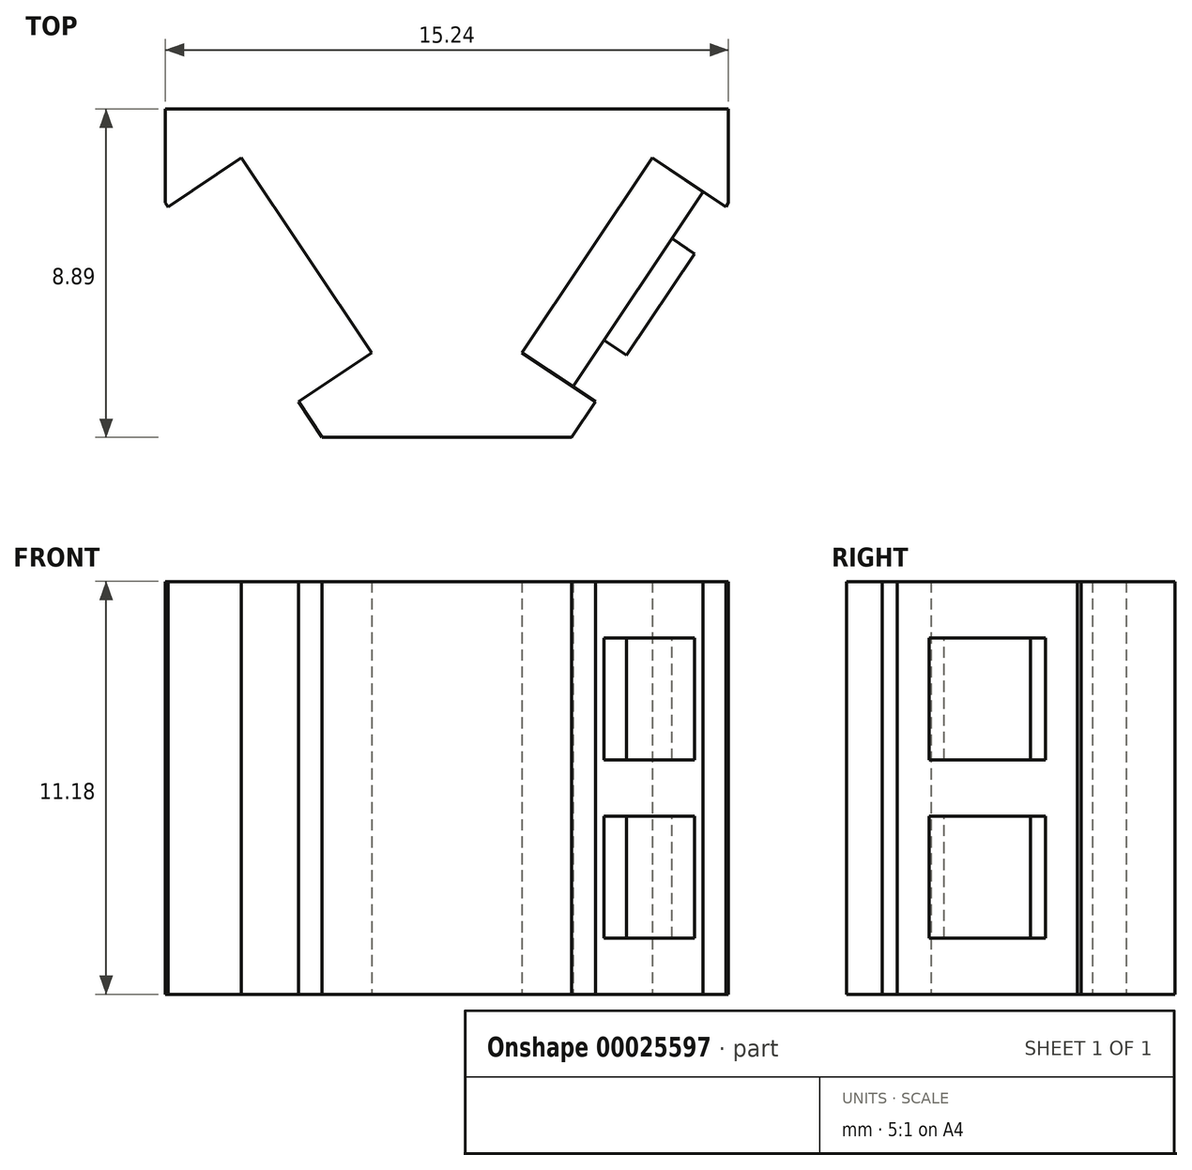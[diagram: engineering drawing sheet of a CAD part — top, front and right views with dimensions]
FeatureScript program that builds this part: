
annotation { "Feature Type Name" : "Feature", "Feature Type Description" : "" }
export const myFeature = defineFeature(function(context is Context, id is Id, definition is map)
    precondition{}
    {
        {
            var Q0;
            Q0=qCreatedBy(makeId("Top.planeOp"),FACE);
            var sketch = newSketch(context, id + "F0", { "sketchPlane" : qUnion([Q0])});
            skLineSegment(sketch, "E0", {"start": v(0, 0) * mm, "end": v(7.62, 0) * mm});
            skLineSegment(sketch, "E1", {"start": v(7.62, 0) * mm, "end": v(7.62, -2.54) * mm});
            skLineSegment(sketch, "E2", {"start": v(7.62, -2.54) * mm, "end": v(7.55, -2.65) * mm});
            skLineSegment(sketch, "E3", {"start": v(3.38, -8.9) * mm, "end": v(0, -8.9) * mm});
            skLineSegment(sketch, "E4", {"start": v(0, -8.9) * mm, "end": v(0, 0) * mm});
            skLineSegment(sketch, "E5", {"start": v(4.02, -7.93) * mm, "end": v(2.03, -6.6) * mm});
            skLineSegment(sketch, "E6", {"start": v(2.03, -6.6) * mm, "end": v(5.56, -1.32) * mm});
            skLineSegment(sketch, "E7", {"start": v(5.56, -1.32) * mm, "end": v(7.55, -2.65) * mm});
            skLineSegment(sketch, "E8.trimOffspring", {"start": v(4.02, -7.93) * mm, "end": v(3.38, -8.89) * mm});
            skSolve(sketch);
        }
        {
            var Q0;
            Q0=makeQuery(id+"F0.imprint","IMPRINT",FACE,{"disambiguationData":[TD([[makeQuery(id+"F0.imprint","IMPRINT",EDGE,{"derivedFrom":sQuery(id+"F0.wireOp",EDGE,"E0")}),-1.0]])]});
            extrude(context, id + "F1", {"entities" : qUnion([Q0]), "depth" : 11.18 * mm});
        }
        {
            var Q0;
            Q0=makeQuery(id+"F1.opExtrude","SWEPT_BODY",BODY,{"disambiguationData":[OSD([sQuery(id+"F0.wireOp",EDGE,"E0"),sQuery(id+"F0.wireOp",EDGE,"E1"),sQuery(id+"F0.wireOp",EDGE,"E2"),sQuery(id+"F0.wireOp",EDGE,"E3"),sQuery(id+"F0.wireOp",EDGE,"E4"),sQuery(id+"F0.wireOp",EDGE,"E5"),sQuery(id+"F0.wireOp",EDGE,"E6"),sQuery(id+"F0.wireOp",EDGE,"E7"),sQuery(id+"F0.wireOp",EDGE,"E8.trimOffspring")])]});
            var Q1;
            Q1=qCreatedBy(makeId("Right.planeOp"),FACE);
            mirror(context, id + "F2", {"operationType" : NewBodyOperationType.ADD, "entities" : qUnion([Q0]), "mirrorPlane" : qUnion([Q1])});
        }
        {
            var Q0;
            Q0=makeQuery(id+"F1.opExtrude","SWEPT_FACE",FACE,{"disambiguationData":[OSD([sQuery(id+"F0.wireOp",EDGE,"E6")])]});
            var sketch = newSketch(context, id + "F3", { "sketchPlane" : qUnion([Q0])});
            skLineSegment(sketch, "E9.bottom", {"start": v(-4.36, 0) * mm, "end": v(2, 0) * mm});
            skLineSegment(sketch, "E9.top", {"start": v(-4.36, 11.18) * mm, "end": v(2, 11.18) * mm});
            skLineSegment(sketch, "E9.left", {"start": v(-4.36, 0) * mm, "end": v(-4.36, 11.18) * mm});
            skLineSegment(sketch, "E9.right", {"start": v(2, 0) * mm, "end": v(2, 11.18) * mm});
            skSolve(sketch);
        }
        {
            var Q0;
            Q0=makeQuery(id+"F3.imprint","IMPRINT",FACE,{"disambiguationData":[TD([[makeQuery(id+"F3.imprint","IMPRINT",EDGE,{"derivedFrom":sQuery(id+"F3.wireOp",EDGE,"E9.bottom")}),1.0]])]});
            extrude(context, id + "F4", {"entities" : qUnion([Q0]), "depth" : 1.65 * mm});
        }
        {
            var Q0;
            Q0=makeQuery(id+"F4.opExtrude","CAP_FACE",FACE,{"disambiguationData":[OSD([sQuery(id+"F3.wireOp",EDGE,"E9.bottom"),sQuery(id+"F3.wireOp",EDGE,"E9.top"),sQuery(id+"F3.wireOp",EDGE,"E9.left"),sQuery(id+"F3.wireOp",EDGE,"E9.right")])],"isStart":false});
            var sketch = newSketch(context, id + "F5", { "sketchPlane" : qUnion([Q0])});
            skLineSegment(sketch, "E10.bottom", {"start": v(-2.84, 1.52) * mm, "end": v(0.47, 1.52) * mm});
            skLineSegment(sketch, "E10.top", {"start": v(-2.84, 4.83) * mm, "end": v(0.47, 4.83) * mm});
            skLineSegment(sketch, "E10.left", {"start": v(-2.84, 1.52) * mm, "end": v(-2.84, 4.83) * mm});
            skLineSegment(sketch, "E10.right", {"start": v(0.47, 1.52) * mm, "end": v(0.47, 4.83) * mm});
            skLineSegment(sketch, "E11.bottom", {"start": v(-2.84, 6.35) * mm, "end": v(0.47, 6.35) * mm});
            skLineSegment(sketch, "E11.top", {"start": v(-2.84, 9.65) * mm, "end": v(0.47, 9.65) * mm});
            skLineSegment(sketch, "E11.left", {"start": v(-2.84, 6.35) * mm, "end": v(-2.84, 9.65) * mm});
            skLineSegment(sketch, "E11.right", {"start": v(0.47, 6.35) * mm, "end": v(0.47, 9.65) * mm});
            skSolve(sketch);
        }
        {
            var Q0;
            Q0=makeQuery(id+"F5.imprint","IMPRINT",FACE,{"disambiguationData":[TD([[makeQuery(id+"F5.imprint","IMPRINT",EDGE,{"derivedFrom":sQuery(id+"F5.wireOp",EDGE,"E11.bottom")}),1.0]])]});
            var Q1;
            Q1=makeQuery(id+"F5.imprint","IMPRINT",FACE,{"disambiguationData":[TD([[makeQuery(id+"F5.imprint","IMPRINT",EDGE,{"derivedFrom":sQuery(id+"F5.wireOp",EDGE,"E10.bottom")}),1.0]])]});
            extrude(context, id + "F6", {"entities" : qUnion([Q0, Q1]), "depth" : 0.74 * mm});
        }
    });
